# Revit family: 2089550(n0300)
name_source: partatom
category: Security Devices
units: mm (PartAtom-declared; Revit-internal decimal feet)

## family parameters
Always vertical = No
Cut with Voids When Loaded = No
Host = Ceiling
OmniClass Number = 23.85.30.14
OmniClass Title = Presence Detection/Registration
Room Calculation Point = No
Shared = Yes

## types (2) — shared parameters
zero-valued in all types: A, EF001992, EF010517

## per-type parameters (varying)
- Type 1: CTN=0; EF000218=0 mm  [stored 0 ft]; EF000259=0; EF000846=0 mm  [stored 0 ft]; EF001322=0 mm  [stored 0 ft]; EF001323=0 mm  [stored 0 ft]; EF003843=0 mm  [stored 0 ft]; EF003882=0; EF004265=0 mm  [stored 0 ft]; EF006589=0; EF006590=0; EF008011=0 mm  [stored 0 ft]; EF010886=0 mm  [stored 0 ft]; EF010945=0 mm  [stored 0 ft]; EF010946=0 mm  [stored 0 ft]; LOG=0; NOCUPEROU=0; PRICEQUANTITY=0; QUANTITYINT=0; QUANTITYMIN=0
- 2089550: ARTICLENO=NB; BOMINFO=LINA; CATALOG=Theben; COO=HU; CTN=90314990; DEEPLINK_PRODUKTSEITE=http://www.theben.de; DESCLONG=KNX presence detector for surface ceiling mounting, KNX interface, detection range 4 m (for sitting persons), 8 m (for walking persons) at 3 m mounting height, mounting height up to 4 m, 2 channels light with light measurement or without brightness influence, 2 channels presence (individually parameterizable), self-learning follow-up time, short-time presence, manual override, Constant light control with orientation light (stand-by functionality), dimmable lighting in switching mode with orientation light (stand-by functionality), brightness setpoint adjustable in lux via parameter, object or remote control, teach-in function, scene functionality, remote control, light measurement 10-3000 lux, simple adjustment of light measurement,sensitivity adjustable, protection class IP 54, housing white; DESCSHORT=KNX presence detector for ceiling mounting surface mount, white; EF000003=EV000384; EF000007=White; EF000010=Presence detector; EF000139=Untreated; EF000147=false; EF000218=1 mm  [stored 0.00328084 ft]; EF000259=3; EF000846=1 mm  [stored 0.00328084 ft]; EF001098=true; EF001257=Thermoplast; EF001322=4000 mm  [stored 13.1234 ft]; EF001323=4000 mm  [stored 13.1234 ft]; EF001499=true; EF001500=false; EF001501=false; EF001504=true; EF002169=Plastic; EF003831=false; EF003843=8000 mm; EF003876=false; EF003882=9010; EF003898=true; EF004265=15 mm  [stored 0.0492126 ft]; EF004530=false; EF006243=false; EF006311=false; EF006569=matt; EF006582=0, 360 °; EF006589=30; EF006590=60; EF007575=true; EF007667=true; EF008011=3000 mm; EF008855=false; EF009466=false; EF010886=58 mm  [stored 0.190289 ft]; EF010945=96 mm  [stored 0.314961 ft]; EF010946=55 mm  [stored 0.180446 ft]; EF016048=false; GEBRAUCHSANLEITUNG=http://www.theben.de; INTNO=7612748006447; LINA=2089550; LOG=300; MANUID=2089550; MANUNAME=Theben AG; MANUTYPEDESC=theRonda S360 KNX AP WH; Manufacturer=Theben; Model=2089550; NB=2089550(N0300); NBSYN=$MANUID.($SA.$A.$LOG.); NN=theRonda S KNX; NOCUPEROU=1; PRICEQUANTITY=1; PRODUKTDATENBLATT=http://www.theben.de; QUANTITYINT=1; QUANTITYMIN=1; REACH_ERKLAERUNG=http://www.theben.de; REMARKS=ERP-GROUP 360; SA=None; SUPPLIER=THEBEN; SUPPLIERALTNO=2089550

note: [stored X ft] marks values corroborated as IEEE doubles in the binary element streams (Revit-internal decimal feet)

## geometry (parser evidence)
native form markers: Sweep x9
no freeform markers — native parametric forms only
